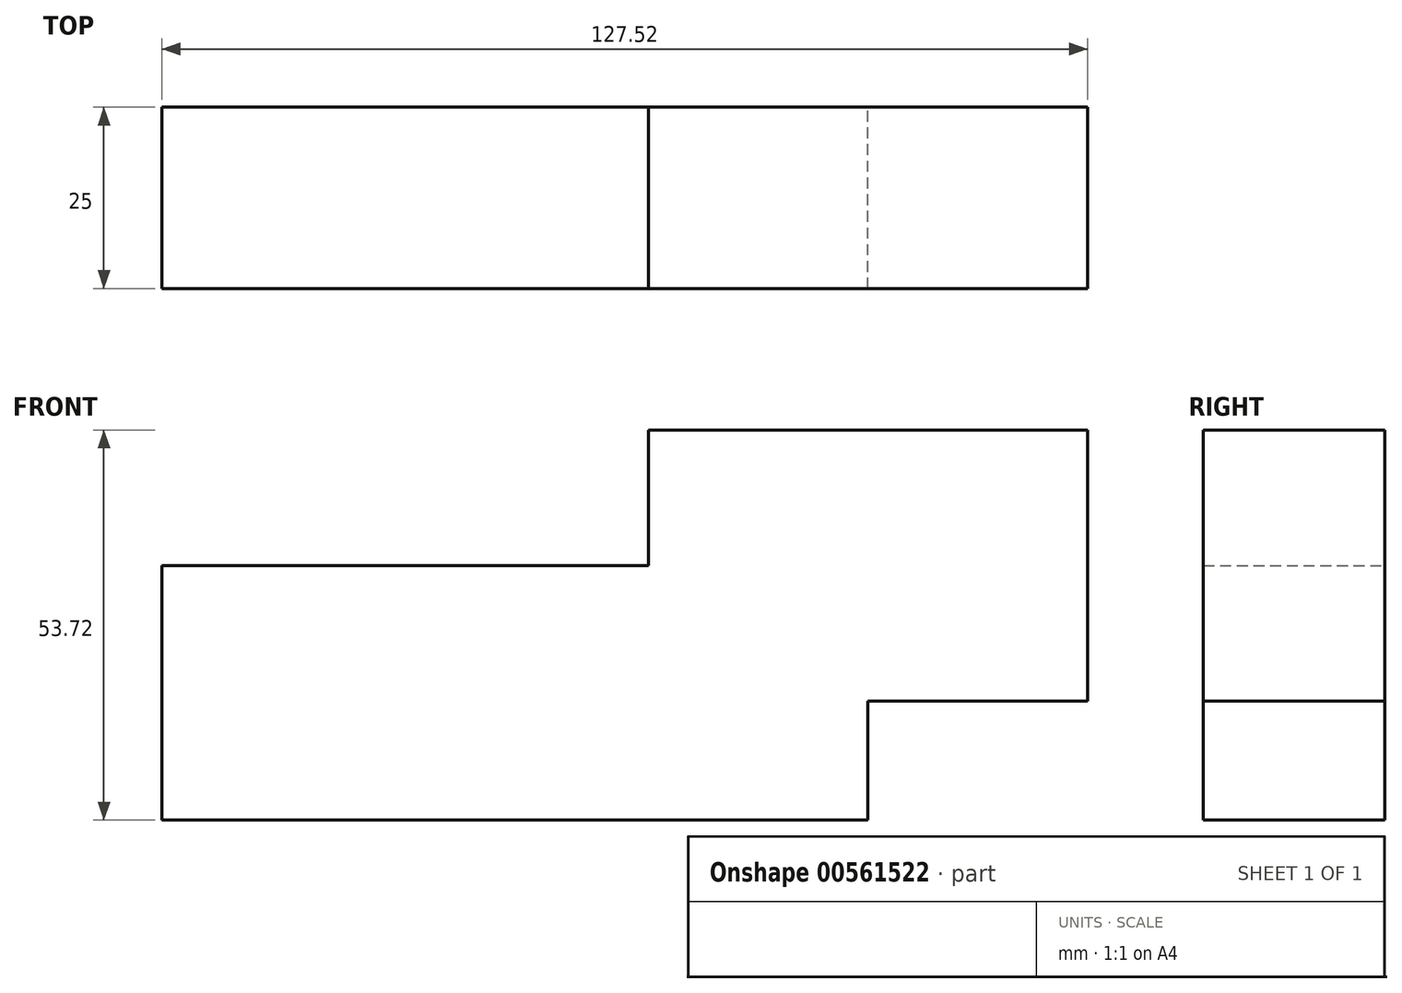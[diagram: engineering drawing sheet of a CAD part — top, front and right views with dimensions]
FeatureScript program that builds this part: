
annotation { "Feature Type Name" : "Feature", "Feature Type Description" : "" }
export const myFeature = defineFeature(function(context is Context, id is Id, definition is map)
    precondition{}
    {
        {
            var Q0;
            Q0=qCreatedBy(makeId("Front.planeOp"),FACE);
            var sketch = newSketch(context, id + "F0", { "sketchPlane" : qUnion([Q0])});
            skLineSegment(sketch, "E0.bottom", {"start": v(45.67, 17.53) * mm, "end": v(-51.6, 17.53) * mm});
            skLineSegment(sketch, "E0.top", {"start": v(45.67, -17.53) * mm, "end": v(-51.6, -17.53) * mm});
            skLineSegment(sketch, "E0.left", {"start": v(45.67, 17.53) * mm, "end": v(45.67, -17.53) * mm});
            skLineSegment(sketch, "E0.right", {"start": v(-51.6, 17.53) * mm, "end": v(-51.6, -17.53) * mm});
            skPoint(sketch, "E0.middle", {"position": v(-2.97, 0) * mm});
            skLineSegment(sketch, "E1.bottom", {"start": v(15.41, 36.2) * mm, "end": v(75.92, 36.2) * mm});
            skLineSegment(sketch, "E1.top", {"start": v(15.41, -1.13) * mm, "end": v(75.92, -1.13) * mm});
            skLineSegment(sketch, "E1.left", {"start": v(15.41, 36.2) * mm, "end": v(15.41, -1.13) * mm});
            skLineSegment(sketch, "E1.right", {"start": v(75.92, 36.2) * mm, "end": v(75.92, -1.13) * mm});
            skPoint(sketch, "E1.middle", {"position": v(45.67, 17.53) * mm});
            skSolve(sketch);
        }
        {
            var Q0;
            Q0 = qSketchRegion(id + "F0", true);
            extrude(context, id + "F1", {"entities" : qUnion([Q0]), "depth" : 25 * mm, "offsetDistance" : 25 * mm, "symmetric" : true});
        }
    });
